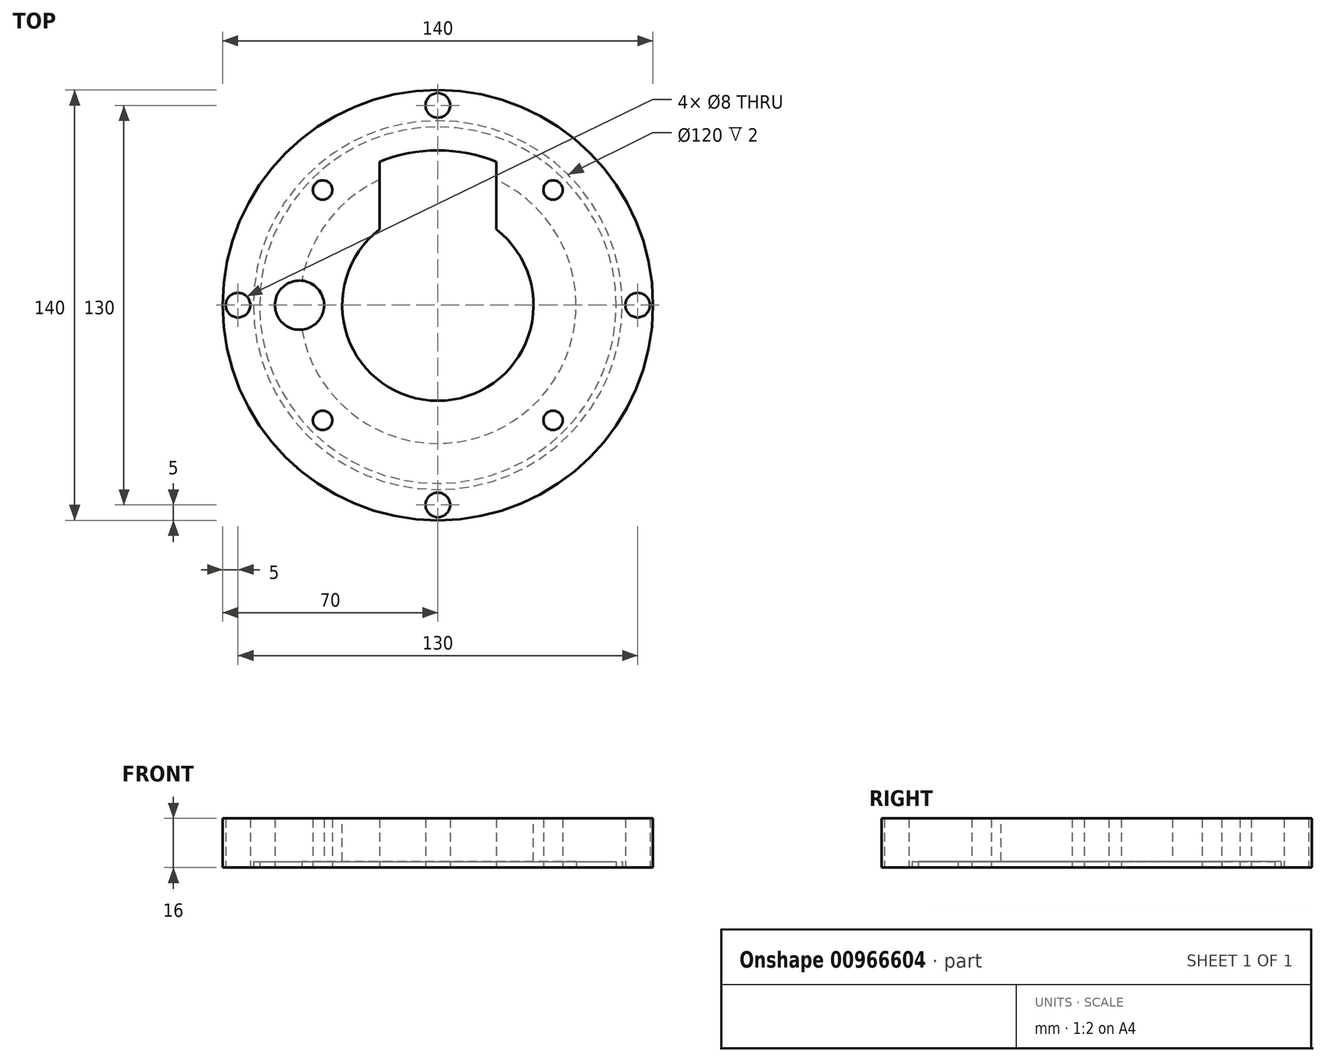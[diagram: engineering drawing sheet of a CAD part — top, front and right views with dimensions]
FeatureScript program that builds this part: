
annotation { "Feature Type Name" : "Feature", "Feature Type Description" : "" }
export const myFeature = defineFeature(function(context is Context, id is Id, definition is map)
    precondition{}
    {
        {
            var Q0;
            Q0=qCreatedBy(makeId("Top.planeOp"),FACE);
            var sketch = newSketch(context, id + "F0", { "sketchPlane" : qUnion([Q0])});
            skCircle(sketch, "E0", {"center": v(0, 0) * mm, "radius": 70 * mm});
            skSolve(sketch);
        }
        {
            var Q0;
            Q0 = qSketchRegion(id + "F0", true);
            extrude(context, id + "F1", {"entities" : qUnion([Q0]), "depth" : 16 * mm, "offsetDistance" : 25 * mm});
        }
        {
            var Q0;
            Q0=makeQuery(id+"F1.opExtrude","CAP_FACE",FACE,{"disambiguationData":[OSD([sQuery(id+"F0.wireOp",EDGE,"E0")])],"isStart":false});
            var sketch = newSketch(context, id + "F2", { "sketchPlane" : qUnion([Q0])});
            skCircle(sketch, "E1", {"center": v(0, 0) * mm, "radius": 31.12 * mm});
            skSolve(sketch);
        }
        {
            var Q0;
            Q0 = qSketchRegion(id + "F2", true);
            extrude(context, id + "F3", {"entities" : qUnion([Q0]), "operationType" : NewBodyOperationType.REMOVE, "endBound" : BoundingType.THROUGH_ALL, "oppositeDirection" : true, "depth" : 25 * mm, "offsetDistance" : 25 * mm});
        }
        {
            var Q0;
            Q0=makeQuery(id+"F1.opExtrude","CAP_FACE",FACE,{"disambiguationData":[OSD([sQuery(id+"F0.wireOp",EDGE,"E0")])],"isStart":true});
            var sketch = newSketch(context, id + "F4", { "sketchPlane" : qUnion([Q0])});
            skArc(sketch, "E2", {"start": v(-19, -46.65) * mm, "mid": v(0, -50.37) * mm, "end": v(19, -46.65) * mm});
            skLineSegment(sketch, "E3", {"start": v(0, 73.04) * mm, "end": v(0, -73.43) * mm, "construction": true});
            skLineSegment(sketch, "E4", {"start": v(-19, -46.65) * mm, "end": v(-19, 0) * mm});
            skLineSegment(sketch, "E5", {"start": v(19, -46.65) * mm, "end": v(19, 0) * mm});
            skLineSegment(sketch, "E6", {"start": v(19, 0) * mm, "end": v(-19, 0) * mm});
            skCircle(sketch, "E7", {"center": v(0, 0) * mm, "radius": 65 * mm, "construction": true});
            skCircle(sketch, "E8", {"center": v(0, 65) * mm, "radius": 4 * mm});
            skCircle(sketch, "E9.1.0", {"center": v(65, 0) * mm, "radius": 4 * mm});
            skCircle(sketch, "E9.2.0", {"center": v(0, -65) * mm, "radius": 4 * mm});
            skCircle(sketch, "E9.3.0", {"center": v(-65, 0) * mm, "radius": 4 * mm});
            skLineSegment(sketch, "E9.anchor1", {"start": v(0, 0) * mm, "end": v(0, 65) * mm, "construction": true});
            skLineSegment(sketch, "E9.anchor2", {"start": v(0, 0) * mm, "end": v(-65, 0) * mm, "construction": true});
            skCircle(sketch, "E10", {"center": v(-45, 0) * mm, "radius": 8 * mm});
            skCircle(sketch, "E11", {"center": v(0, 0) * mm, "radius": 53 * mm, "construction": true});
            skLineSegment(sketch, "E12.bottom", {"start": v(-37.48, 37.48) * mm, "end": v(37.48, 37.48) * mm, "construction": true});
            skLineSegment(sketch, "E12.top", {"start": v(-37.48, -37.48) * mm, "end": v(37.48, -37.48) * mm, "construction": true});
            skLineSegment(sketch, "E12.left", {"start": v(-37.48, 37.48) * mm, "end": v(-37.48, -37.48) * mm, "construction": true});
            skLineSegment(sketch, "E12.right", {"start": v(37.48, 37.48) * mm, "end": v(37.48, -37.48) * mm, "construction": true});
            skCircle(sketch, "E13", {"center": v(-37.48, 37.48) * mm, "radius": 3.15 * mm});
            skCircle(sketch, "E14", {"center": v(37.48, 37.48) * mm, "radius": 3.15 * mm});
            skCircle(sketch, "E15", {"center": v(37.48, -37.48) * mm, "radius": 3.15 * mm});
            skCircle(sketch, "E16", {"center": v(-37.48, -37.48) * mm, "radius": 3.15 * mm});
            skCircle(sketch, "E17.0", {"center": v(0, 0) * mm, "radius": 31.12 * mm});
            skCircle(sketch, "E18", {"center": v(0, 0) * mm, "radius": 70 * mm});
            skLineSegment(sketch, "E19", {"start": v(-19, -24.65) * mm, "end": v(19, -24.65) * mm, "construction": true});
            skSolve(sketch);
        }
        {
            var Q0;
            {var subQ0=sQuery(id+"F4.wireOp",EDGE,"E2");Q0=makeQuery(id+"F4.imprint","IMPRINT",FACE,{"disambiguationData":[TD([[makeQuery(id+"F4.imprint","IMPRINT",EDGE,{"derivedFrom":subQ0}),1.0]])]});}
            var Q1;
            Q1=makeQuery(id+"F4.imprint","IMPRINT",FACE,{"disambiguationData":[TD([[makeQuery(id+"F4.imprint","IMPRINT",EDGE,{"derivedFrom":sQuery(id+"F4.wireOp",EDGE,"E16")}),1.0]])]});
            var Q2;
            Q2=makeQuery(id+"F4.imprint","IMPRINT",FACE,{"disambiguationData":[TD([[makeQuery(id+"F4.imprint","IMPRINT",EDGE,{"derivedFrom":sQuery(id+"F4.wireOp",EDGE,"E10")}),1.0]])]});
            var Q3;
            Q3=makeQuery(id+"F4.imprint","IMPRINT",FACE,{"disambiguationData":[TD([[makeQuery(id+"F4.imprint","IMPRINT",EDGE,{"derivedFrom":sQuery(id+"F4.wireOp",EDGE,"E9.3.0")}),1.0]])]});
            var Q4;
            Q4=makeQuery(id+"F4.imprint","IMPRINT",FACE,{"disambiguationData":[TD([[makeQuery(id+"F4.imprint","IMPRINT",EDGE,{"derivedFrom":sQuery(id+"F4.wireOp",EDGE,"E13")}),1.0]])]});
            var Q5;
            Q5=makeQuery(id+"F4.imprint","IMPRINT",FACE,{"disambiguationData":[TD([[makeQuery(id+"F4.imprint","IMPRINT",EDGE,{"derivedFrom":sQuery(id+"F4.wireOp",EDGE,"E14")}),1.0]])]});
            var Q6;
            Q6=makeQuery(id+"F4.imprint","IMPRINT",FACE,{"disambiguationData":[TD([[makeQuery(id+"F4.imprint","IMPRINT",EDGE,{"derivedFrom":sQuery(id+"F4.wireOp",EDGE,"E15")}),1.0]])]});
            var Q7;
            Q7=makeQuery(id+"F4.imprint","IMPRINT",FACE,{"disambiguationData":[TD([[makeQuery(id+"F4.imprint","IMPRINT",EDGE,{"derivedFrom":sQuery(id+"F4.wireOp",EDGE,"E9.1.0")}),1.0]])]});
            var Q8;
            Q8=makeQuery(id+"F4.imprint","IMPRINT",FACE,{"disambiguationData":[TD([[makeQuery(id+"F4.imprint","IMPRINT",EDGE,{"derivedFrom":sQuery(id+"F4.wireOp",EDGE,"E8")}),1.0]])]});
            var Q9;
            Q9=makeQuery(id+"F4.imprint","IMPRINT",FACE,{"disambiguationData":[TD([[makeQuery(id+"F4.imprint","IMPRINT",EDGE,{"derivedFrom":sQuery(id+"F4.wireOp",EDGE,"E9.2.0")}),1.0]])]});
            extrude(context, id + "F5", {"entities" : qUnion([Q0, Q1, Q2, Q3, Q4, Q5, Q6, Q7, Q8, Q9]), "operationType" : NewBodyOperationType.REMOVE, "endBound" : BoundingType.THROUGH_ALL, "oppositeDirection" : true, "depth" : 25 * mm, "offsetDistance" : 25 * mm});
        }
        {
            var Q0;
            Q0=makeQuery(id+"F1.opExtrude","CAP_FACE",FACE,{"disambiguationData":[OSD([sQuery(id+"F0.wireOp",EDGE,"E0")])],"isStart":true});
            var sketch = newSketch(context, id + "F6", { "sketchPlane" : qUnion([Q0])});
            skCircle(sketch, "E20", {"center": v(0, 0) * mm, "radius": 45 * mm});
            skSolve(sketch);
        }
        {
            var Q0;
            Q0 = qSketchRegion(id + "F6", true);
            extrude(context, id + "F7", {"entities" : qUnion([Q0]), "operationType" : NewBodyOperationType.REMOVE, "oppositeDirection" : true, "depth" : 2 * mm, "offsetDistance" : 25 * mm});
        }
        {
            var Q0;
            Q0=makeQuery(id+"F1.opExtrude","CAP_FACE",FACE,{"disambiguationData":[OSD([sQuery(id+"F0.wireOp",EDGE,"E0")])],"isStart":true});
            var sketch = newSketch(context, id + "F8", { "sketchPlane" : qUnion([Q0])});
            skCircle(sketch, "E21", {"center": v(0, 0) * mm, "radius": 58 * mm});
            skCircle(sketch, "E22", {"center": v(0, 0) * mm, "radius": 60 * mm});
            skSolve(sketch);
        }
        {
            var Q0;
            Q0 = qSketchRegion(id + "F8", true);
            extrude(context, id + "F9", {"entities" : qUnion([Q0]), "operationType" : NewBodyOperationType.REMOVE, "oppositeDirection" : true, "depth" : 2 * mm, "offsetDistance" : 25 * mm});
        }
    });
